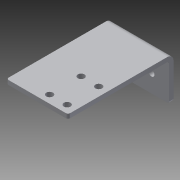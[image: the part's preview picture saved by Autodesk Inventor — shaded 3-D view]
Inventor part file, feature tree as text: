
AUTODESK INVENTOR PART (.ipt)
format: ipt  version: 2014 (Build 180170000, 170)  size: 129,536 bytes
history: native  units: in
note: dims shown in document units (in); Inventor stores cm internally (conversion verified against a paired STEP export)
features: sheet_metal_op x4, sketch x3, other x2, fillet x1, extrude x1
ambient origin geometry x8: Origin, YZ Plane, XZ Plane, XY Plane, X Axis, Y Axis, Z Axis, Center Point
bodies: Solid1 (feature_tree)
feature tree (11):
  sheet_metal_op  "Face1"
  sheet_metal_op  "Flange1"
  fillet  "Fillet1"  Radius=1.75in
  extrude  "Extrusion1"  Depth=0.163in
  sketch  "Sketch1"  dims[d1=1.0in d2=0.163in]
  other  "Plate1"
  sketch  "Sketch2"  dims[d4=0.7874in d6=1.0in d7=0.3937in d9=1.0in]
  other  "Plate2"
  sheet_metal_op  "Bend1"
  sheet_metal_op  "Corner1"
  sketch  "Sketch3"  dims[d11=0.125in d12=0.125in d13=0.0625in d14=0.25in d15=0.125in d16=3.0in d17=90.0deg d18=0.05in d19=0.5in d20=0.125in d21=0.125in d22=0.0625in d23=1.35in d24=0.75in d27=0.19in d28=0.125in d29=0.2265in d30=1.0in d31=0.0in d34=0.25in d35=0.875in]
